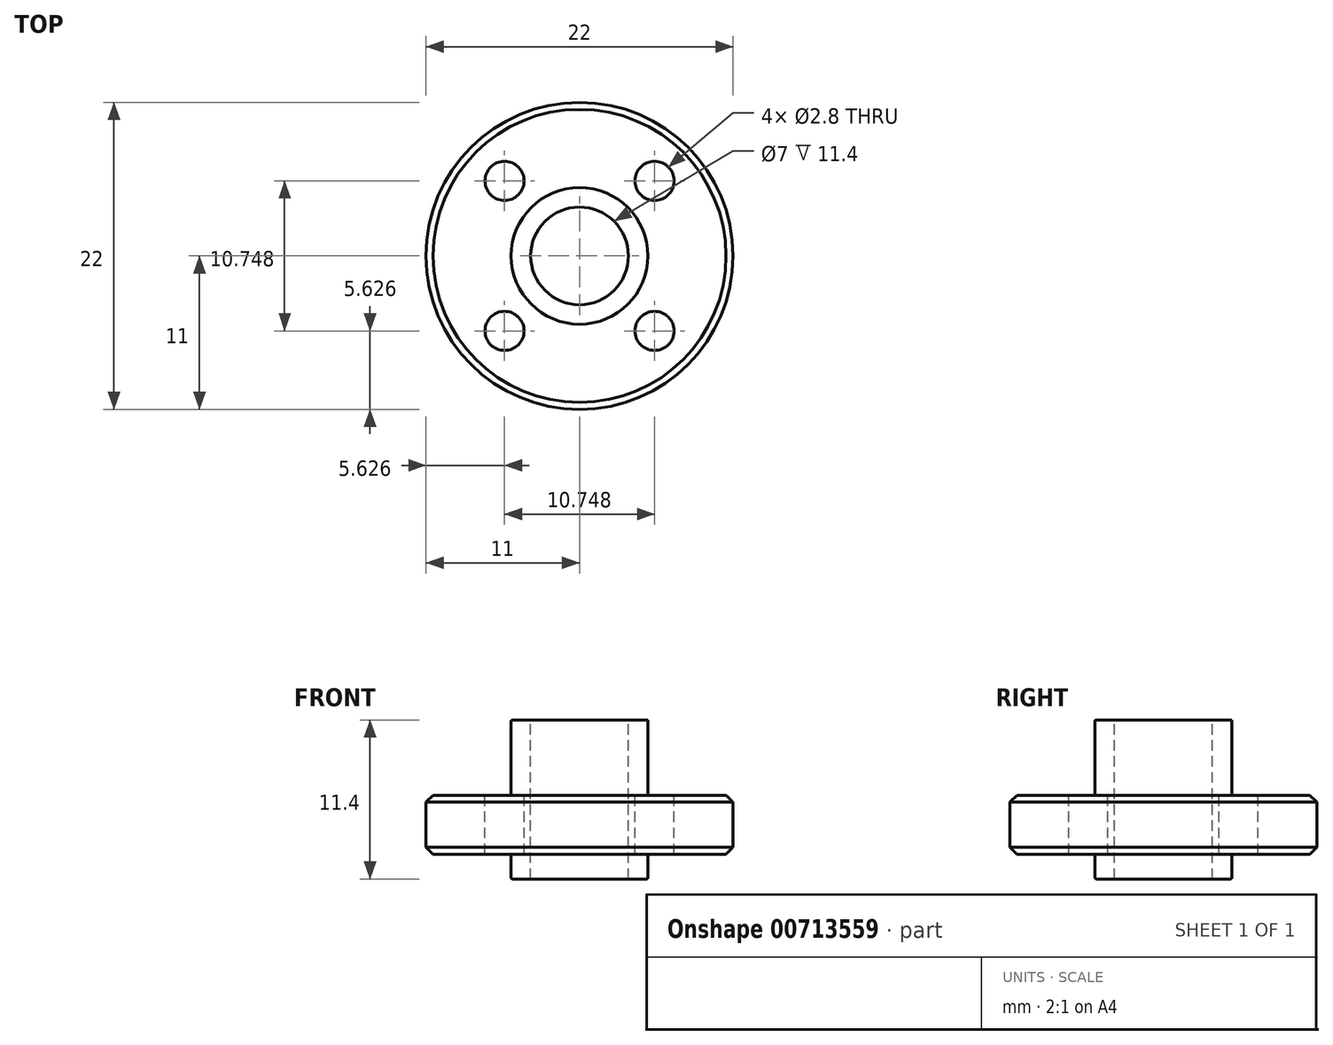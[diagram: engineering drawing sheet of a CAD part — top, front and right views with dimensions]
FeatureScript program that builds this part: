
annotation { "Feature Type Name" : "Feature", "Feature Type Description" : "" }
export const myFeature = defineFeature(function(context is Context, id is Id, definition is map)
    precondition{}
    {
        {
            var Q0;
            Q0=qCreatedBy(makeId("Top.planeOp"),FACE);
            var sketch = newSketch(context, id + "F0", { "sketchPlane" : qUnion([Q0])});
            skCircle(sketch, "E0", {"center": v(0, 0) * mm, "radius": 4.9 * mm});
            skCircle(sketch, "E1", {"center": v(0, 0) * mm, "radius": 11 * mm});
            skLineSegment(sketch, "E2", {"start": v(-7.78, 7.78) * mm, "end": v(7.78, -7.78) * mm, "construction": true});
            skLineSegment(sketch, "E3", {"start": v(-7.78, -7.78) * mm, "end": v(7.78, 7.78) * mm, "construction": true});
            skCircle(sketch, "E4", {"center": v(-5.37, 5.37) * mm, "radius": 1.4 * mm});
            skCircle(sketch, "E5", {"center": v(5.37, 5.37) * mm, "radius": 1.4 * mm});
            skCircle(sketch, "E6", {"center": v(5.37, -5.37) * mm, "radius": 1.4 * mm});
            skCircle(sketch, "E7", {"center": v(-5.37, -5.37) * mm, "radius": 1.4 * mm});
            skCircle(sketch, "E8", {"center": v(0, 0) * mm, "radius": 3.5 * mm});
            skCircle(sketch, "E9", {"center": v(0, 0) * mm, "radius": 7.6 * mm, "construction": true});
            skSolve(sketch);
        }
        {
            var Q0;
            Q0=makeQuery(id+"F0.imprint","IMPRINT",FACE,{"disambiguationData":[TD([[makeQuery(id+"F0.imprint","IMPRINT",EDGE,{"derivedFrom":sQuery(id+"F0.wireOp",EDGE,"E0")}),-1.0]])]});
            var Q1;
            Q1=makeQuery(id+"F0.imprint","IMPRINT",FACE,{"disambiguationData":[TD([[makeQuery(id+"F0.imprint","IMPRINT",EDGE,{"derivedFrom":sQuery(id+"F0.wireOp",EDGE,"E0")}),1.0]])]});
            extrude(context, id + "F1", {"entities" : qUnion([Q0, Q1]), "oppositeDirection" : true, "depth" : 4.22 * mm});
        }
        {
            var Q0;
            Q0=makeQuery(id+"F0.imprint","IMPRINT",FACE,{"disambiguationData":[TD([[makeQuery(id+"F0.imprint","IMPRINT",EDGE,{"derivedFrom":sQuery(id+"F0.wireOp",EDGE,"E0")}),1.0]])]});
            extrude(context, id + "F2", {"entities" : qUnion([Q0]), "operationType" : NewBodyOperationType.ADD, "depth" : 5.4 * mm, "hasSecondDirection" : true, "secondDirectionOppositeDirection" : true, "secondDirectionDepth" : 6 * mm});
        }
        {
            var Q0;
            Q0=makeQuery(id+"F1.opExtrude","CAP_EDGE",EDGE,{"disambiguationData":[OSD([sQuery(id+"F0.wireOp",EDGE,"E1")])],"isStart":true});
            var Q1;
            Q1=makeQuery(id+"F1.opExtrude","CAP_EDGE",EDGE,{"disambiguationData":[OSD([sQuery(id+"F0.wireOp",EDGE,"E1")])],"isStart":false});
            chamfer(context, id + "F3", {"entities" : qUnion([Q0, Q1]), "width" : 0.5 * mm, "tangentPropagation" : true});
        }
        {
            var Q0;
            Q0=makeQuery(id+"F2.opExtrude","CAP_EDGE",EDGE,{"disambiguationData":[OSD([sQuery(id+"F0.wireOp",EDGE,"E0")])],"isStart":false});
            var Q1;
            Q1=makeQuery(id+"F2.boolean.opBoolean","INTERSECT",EDGE,{"derivedFrom":[makeQuery(id+"F1.opExtrude","CAP_FACE",FACE,{"disambiguationData":[OSD([sQuery(id+"F0.wireOp",EDGE,"E1"),sQuery(id+"F0.wireOp",EDGE,"E4"),sQuery(id+"F0.wireOp",EDGE,"E5"),sQuery(id+"F0.wireOp",EDGE,"E6"),sQuery(id+"F0.wireOp",EDGE,"E7"),sQuery(id+"F0.wireOp",EDGE,"E8")])],"isStart":true}),makeQuery(id+"F2.opExtrude","SWEPT_FACE",FACE,{"disambiguationData":[OSD([sQuery(id+"F0.wireOp",EDGE,"E0")])]})]});
            var Q2;
            Q2=makeQuery(id+"F2.boolean.opBoolean","INTERSECT",EDGE,{"derivedFrom":[makeQuery(id+"F1.opExtrude","CAP_FACE",FACE,{"disambiguationData":[OSD([sQuery(id+"F0.wireOp",EDGE,"E1"),sQuery(id+"F0.wireOp",EDGE,"E4"),sQuery(id+"F0.wireOp",EDGE,"E5"),sQuery(id+"F0.wireOp",EDGE,"E6"),sQuery(id+"F0.wireOp",EDGE,"E7"),sQuery(id+"F0.wireOp",EDGE,"E8")])],"isStart":false}),makeQuery(id+"F2.opExtrude","SWEPT_FACE",FACE,{"disambiguationData":[OSD([sQuery(id+"F0.wireOp",EDGE,"E0")])]})]});
            var Q3;
            Q3=makeQuery(id+"F2.opExtrude","CAP_EDGE",EDGE,{"disambiguationData":[OSD([sQuery(id+"F0.wireOp",EDGE,"E0")])],"isStart":true});
            fillet(context, id + "F4", {"entities" : qUnion([Q0, Q1, Q2, Q3]), "radius" : 0.1 * mm, "tangentPropagation" : true, "allowEdgeOverflow" : false});
        }
    });
